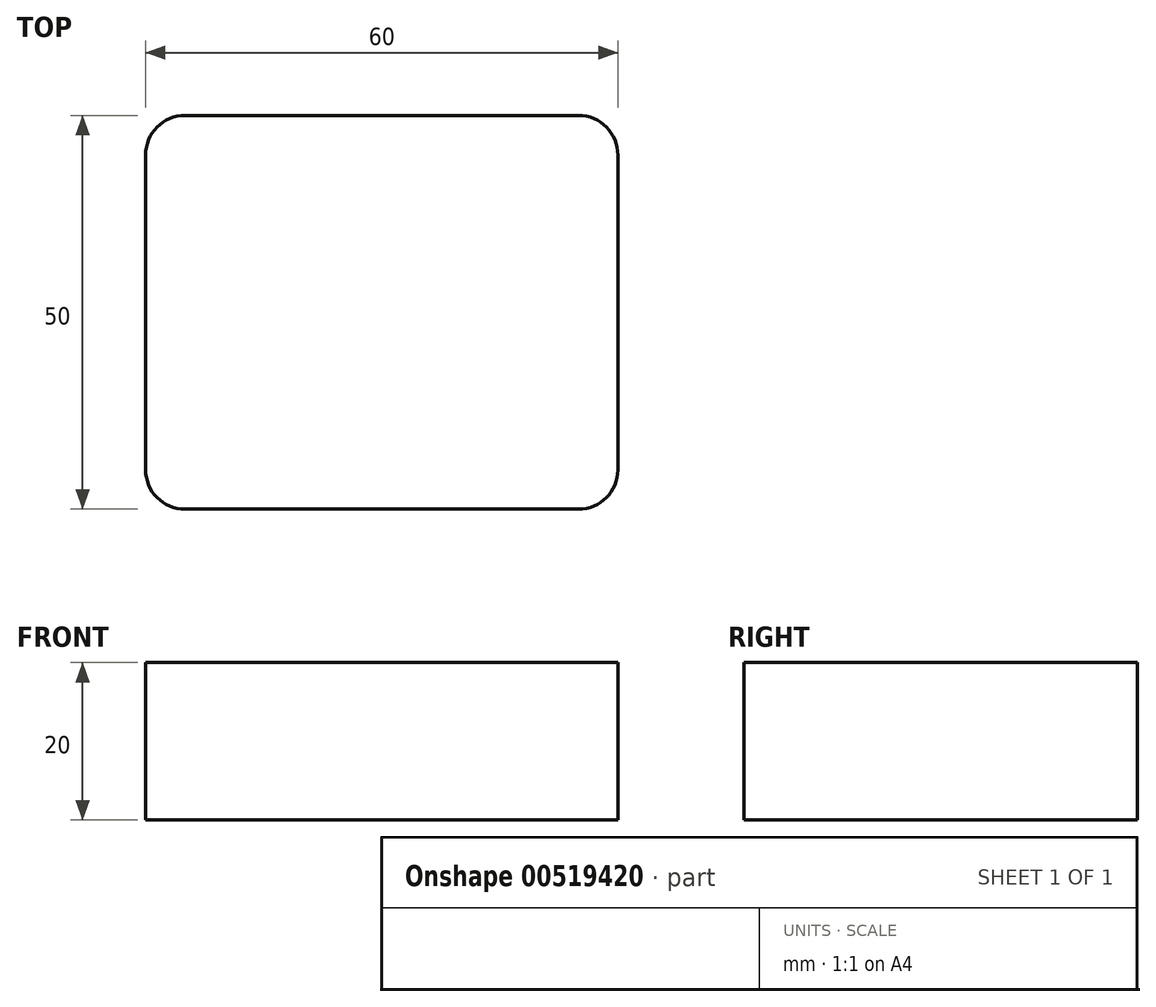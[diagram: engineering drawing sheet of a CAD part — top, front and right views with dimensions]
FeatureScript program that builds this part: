
annotation { "Feature Type Name" : "Feature", "Feature Type Description" : "" }
export const myFeature = defineFeature(function(context is Context, id is Id, definition is map)
    precondition{}
    {
        {
            var Q0;
            Q0=qCreatedBy(makeId("Top.planeOp"),FACE);
            var sketch = newSketch(context, id + "F0", { "sketchPlane" : qUnion([Q0])});
            skLineSegment(sketch, "E0.bottom", {"start": v(1.8, 22.42) * mm, "end": v(51.8, 22.42) * mm});
            skLineSegment(sketch, "E0.top", {"start": v(1.8, -27.58) * mm, "end": v(51.8, -27.58) * mm});
            skLineSegment(sketch, "E0.left", {"start": v(-3.2, 17.42) * mm, "end": v(-3.2, -22.58) * mm});
            skLineSegment(sketch, "E0.right", {"start": v(56.8, 17.42) * mm, "end": v(56.8, -22.58) * mm});
            skPoint(sketch, "E1.visualSharp", {"position": v(-3.2, 22.42) * mm});
            skArc(sketch, "E1.filletArc", {"start": v(1.8, 22.42) * mm, "mid": v(-1.73, 20.95) * mm, "end": v(-3.2, 17.42) * mm});
            skPoint(sketch, "E2.visualSharp", {"position": v(56.8, 22.42) * mm});
            skArc(sketch, "E2.filletArc", {"start": v(56.8, 17.42) * mm, "mid": v(55.34, 20.95) * mm, "end": v(51.8, 22.42) * mm});
            skPoint(sketch, "E3.visualSharp", {"position": v(-3.2, -27.58) * mm});
            skArc(sketch, "E3.filletArc", {"start": v(-3.2, -22.58) * mm, "mid": v(-1.73, -26.12) * mm, "end": v(1.8, -27.58) * mm});
            skPoint(sketch, "E4.visualSharp", {"position": v(56.8, -27.58) * mm});
            skArc(sketch, "E4.filletArc", {"start": v(51.8, -27.58) * mm, "mid": v(55.34, -26.12) * mm, "end": v(56.8, -22.58) * mm});
            skSolve(sketch);
        }
        {
            var Q0;
            Q0=makeQuery(id+"F0.imprint","IMPRINT",FACE,{"disambiguationData":[TD([[makeQuery(id+"F0.imprint","IMPRINT",EDGE,{"derivedFrom":sQuery(id+"F0.wireOp",EDGE,"E0.bottom")}),-1.0]])]});
            extrude(context, id + "F1", {"entities" : qUnion([Q0]), "depth" : 20 * mm, "offsetDistance" : 25.4 * mm});
        }
    });
